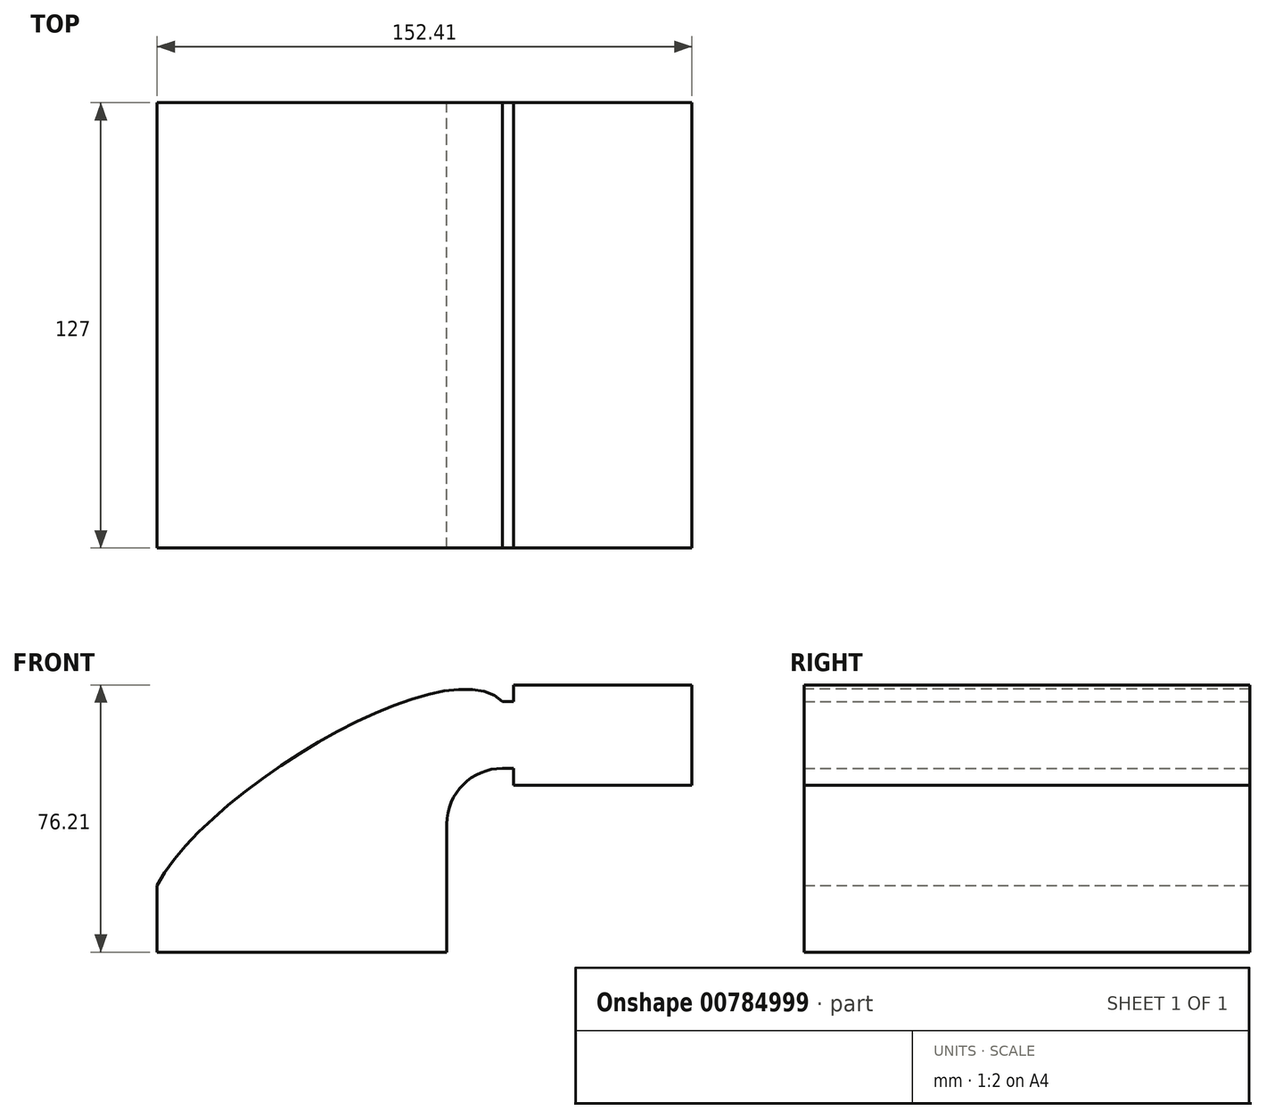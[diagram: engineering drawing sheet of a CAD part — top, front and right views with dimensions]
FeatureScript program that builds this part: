
annotation { "Feature Type Name" : "Feature", "Feature Type Description" : "" }
export const myFeature = defineFeature(function(context is Context, id is Id, definition is map)
    precondition{}
    {
        {
            var Q0;
            Q0=qCreatedBy(makeId("Front.planeOp"),FACE);
            var sketch = newSketch(context, id + "F0", { "sketchPlane" : qUnion([Q0])});
            skLineSegment(sketch, "E0.bottom", {"start": v(-41.28, -9.53) * mm, "end": v(41.28, -9.53) * mm});
            skLineSegment(sketch, "E0.top", {"start": v(-41.28, 9.53) * mm, "end": v(41.28, 9.53) * mm});
            skLineSegment(sketch, "E0.left", {"start": v(-41.28, -9.53) * mm, "end": v(-41.28, 9.53) * mm});
            skLineSegment(sketch, "E0.right", {"start": v(41.28, -9.53) * mm, "end": v(41.28, 9.53) * mm});
            skPoint(sketch, "E0.middle", {"position": v(0, 0) * mm});
            skLineSegment(sketch, "E1", {"start": v(41.28, 9.52) * mm, "end": v(41.28, 27) * mm});
            skArc(sketch, "E2", {"start": v(41.27, 27) * mm, "mid": v(45.92, 38.23) * mm, "end": v(57.15, 42.88) * mm});
            skLineSegment(sketch, "E3", {"start": v(57.15, 42.88) * mm, "end": v(85.96, 42.88) * mm});
            skLineSegment(sketch, "E4.bottom", {"start": v(111.13, 38.1) * mm, "end": v(60.33, 38.1) * mm});
            skLineSegment(sketch, "E4.top", {"start": v(111.13, 66.67) * mm, "end": v(60.33, 66.67) * mm});
            skLineSegment(sketch, "E4.left", {"start": v(111.13, 38.1) * mm, "end": v(111.13, 66.68) * mm});
            skLineSegment(sketch, "E4.right", {"start": v(60.33, 38.1) * mm, "end": v(60.33, 66.67) * mm});
            skPoint(sketch, "E4.middle", {"position": v(85.73, 52.39) * mm});
            skLineSegment(sketch, "E5.0", {"start": v(57.15, 61.93) * mm, "end": v(85.96, 61.93) * mm});
            skArc(sketch, "E5.1", {"start": v(22.22, 27) * mm, "mid": v(32.45, 51.7) * mm, "end": v(57.15, 61.93) * mm});
            skLineSegment(sketch, "E5.2", {"start": v(22.22, 9.52) * mm, "end": v(22.22, 27) * mm});
            skLineSegment(sketch, "E6", {"start": v(85.96, 38.1) * mm, "end": v(85.96, 66.67) * mm});
            skFitSpline(sketch, "E7", {"points": [v(-41.28, 9.53) * mm, v(57.15, 61.93) * mm], "startDerivative": vector(42.99, 82.04) * mm, "endDerivative": vector(47.28, -47.35) * mm});
            skSolve(sketch);
        }
        {
            var Q0;
            Q0 = qSketchRegion(id + "F0", true);
            extrude(context, id + "F1", {"entities" : qUnion([Q0]), "endBound" : BoundingType.SYMMETRIC, "depth" : 127 * mm, "offsetDistance" : 25.4 * mm});
        }
    });
